# Revit family: Arboles UK - 902103CW-WAWA - Fixed Swan Neck Cold Water Removable Nozzle Lever Action
name_source: partatom
category: Plumbing Fixtures
revit_build: Autodesk Revit 2015 (Build: 20140606_1530(x64)
units: mm (PartAtom-declared; Revit-internal decimal feet)

## types (2) — shared parameters
Base to nozzle = 200mm
Colour = White RAL 9016
Default Elevation = 1219 mm
Depth = 155mm
Material = Brass with Rilsan plastic coated
Overall height = 325mm
Pressure = 100PSI
Shank = 1/2" BSP x 60mm Long flat ended
Spare nozzle = Pt No 900130
Standout = 130mm
Width = 100mm

## per-type parameters (varying)
| type | Description | Spare Handwheel | Spare headwork |
| 902103CW-WA | Bench mounted removable nozzle swanneck tap, right hand cold water WRAS | Pt No 960200 | Pt No 950148 |
| 902103CW-WAWA | Bench mounted removable nozzle swanneck tap, right hand cold water WRAS, Lever action | Pt No 190002 | Pt No 950149 |

note: column(s) folded — value = type name in every type: Model

## geometry (parser evidence)
native form markers: Sweep x28
no freeform markers — native parametric forms only
